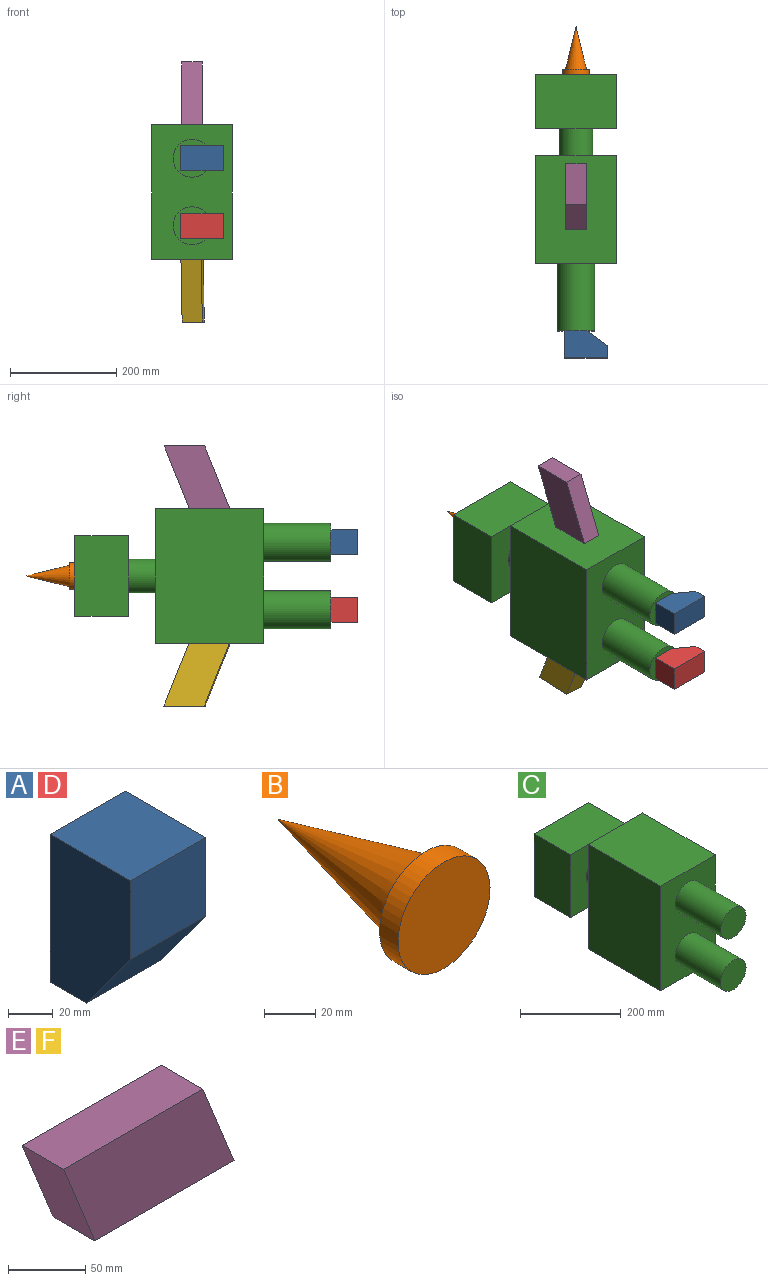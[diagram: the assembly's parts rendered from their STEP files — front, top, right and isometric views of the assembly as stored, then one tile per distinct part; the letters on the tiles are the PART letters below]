
ASSEMBLY  parts=6 mates=5
PART A: 7 faces, bbox 47.2x50.8x80.6 mm
  f0: plane 80.6x50.8mm, normal (-1,0,0), area 3564.2mm2, adj f1,f2,f4,f5,f6
  f1: plane 50.8x47.22mm, normal (0,0,1), area 2398.7mm2, adj f0,f3,f4,f5
  f2: plane 47.22x22.7mm, normal (0,0,-1), area 1071.9mm2, adj f0,f3,f5,f6
  f3: plane 80.6x50.8mm, normal (1,0,0), area 3564.2mm2, adj f1,f2,f4,f5,f6
  f4: plane 47.22x42.87mm, normal (0,-1,0), area 2024.1mm2, adj f0,f1,f3,f6
  f5: plane 80.6x47.22mm, normal (0,1,0), area 3805.6mm2, adj f0,f1,f2,f3
  f6: plane 47.22x37.73mm, normal (0,-0.8,-0.6), area 2221.3mm2, adj f0,f2,f3,f4
PART B: 4 faces, bbox 50.8x91.6x50.8 mm
  f0: cylinder r=25.4mm len=50.8mm, axis (0,1,0), area 1621.5mm2, adj f1,f2
  f1: plane 50.8x50.8mm, normal (0,-1,0), area 2026.8mm2, adj f0
  f2: plane 50.8x50.8mm, normal (0,1,0), area 781.1mm2, adj f0,f3
  f3: cone r=19.91mm half-angle=13.7deg, axis (0,-1,0), area 5247.5mm2, adj f2
PART C: 17 faces, bbox 152.4x482.6x254 mm
  f0: plane 152.4x101.6mm, normal (0,0,1), area 15483.8mm2, adj f1,f3,f4,f5
  f1: plane 152.4x101.6mm, normal (-1,0,0), area 15483.8mm2, adj f0,f2,f4,f5
  f2: plane 152.4x101.6mm, normal (0,0,-1), area 15483.8mm2, adj f1,f3,f4,f5
  f3: plane 152.4x101.6mm, normal (1,0,0), area 15483.8mm2, adj f0,f2,f4,f5
  f4: plane 152.4x152.4mm, normal (0,-1,0), area 20058.8mm2, adj f0,f1,f2,f3,f6
  f5: plane 152.4x152.4mm, normal (0,1,0), area 23225.8mm2, adj f0,f1,f2,f3
  f6: cylinder r=31.75mm len=63.5mm, axis (0,1,0), area 10134.1mm2, adj f4,f12
  f7: plane 203.2x152.4mm, normal (0,0,1), area 30967.7mm2, adj f8,f10,f11,f12
  f8: plane 254x203.2mm, normal (-1,0,0), area 51612.8mm2, adj f7,f9,f11,f12
  f9: plane 203.2x152.4mm, normal (0,0,-1), area 30967.7mm2, adj f8,f10,f11,f12
  f10: plane 254x203.2mm, normal (1,0,0), area 51612.8mm2, adj f7,f9,f11,f12
  f11: plane 254x152.4mm, normal (0,-1,0), area 30764.4mm2, adj f7,f8,f9,f10,f13,f15
  f12: plane 254x152.4mm, normal (0,1,0), area 35542.7mm2, adj f6,f7,f8,f9,f10
  f13: cylinder r=35.56mm len=127mm, axis (0,1,0), area 28375.6mm2, adj f11,f14
  f14: plane 71.12x71.12mm, normal (0,-1,0), area 3972.6mm2, adj f13
  f15: cylinder r=35.56mm len=127mm, axis (0,1,0), area 28375.6mm2, adj f11,f16
  f16: plane 71.12x71.12mm, normal (0,-1,0), area 3972.6mm2, adj f15
PART D: same geometry as A
PART E: 6 faces, bbox 155.4x38.1x70.7 mm
  f0: plane 127x38.1mm, normal (0,0,-1), area 4838.7mm2, adj f1,f3,f4,f5
  f1: plane 70.71x38.1mm, normal (0.93,0,0.37), area 2903.2mm2, adj f0,f2,f4,f5
  f2: plane 127x38.1mm, normal (0,0,1), area 4838.7mm2, adj f1,f3,f4,f5
  f3: plane 70.71x38.1mm, normal (-0.93,0,-0.37), area 2903.2mm2, adj f0,f2,f4,f5
  f4: plane 155.4x70.71mm, normal (0,-1,0), area 8980.3mm2, adj f0,f1,f2,f3
  f5: plane 155.4x70.71mm, normal (0,1,0), area 8980.3mm2, adj f0,f1,f2,f3
PART F: same geometry as E
PLACE A rot(axis=(-0.71,0,0.71),180deg) t=(18.86,-533.4,63.5)mm
PLACE B rot(axis=(1,0,0),0deg) t=(0,10.16,0)mm
PLACE C rot(axis=(1,0,0),0deg) t=(0,0,0)mm fixed
PLACE D rot(axis=(-0.71,0,0.71),180deg) t=(18.86,-533.4,-63.5)mm
PLACE E rot(axis=(0.49,-0.49,0.72),108.3deg) t=(-19.05,-205.73,205.45)mm
PLACE F rot(axis=(-0.49,-0.47,-0.73),110.3deg) t=(18.98,-255.85,-166.4)mm
MATE revolute F.f1 <-> C.f9  axis (0,0,1) through (0,-254,-127)mm
MATE fastened A.f4 <-> C.f15  axis (0,1,0) through (0,-482.6,63.5)mm
MATE revolute E.f3 <-> C.f7  axis (0,0,-1) through (0,-254,127)mm
MATE fastened B.f0 <-> C.f6  axis (0,-1,0) through (0,0,0)mm
MATE fastened D.f4 <-> C.f13  axis (0,1,0) through (0,-482.6,-63.5)mm
